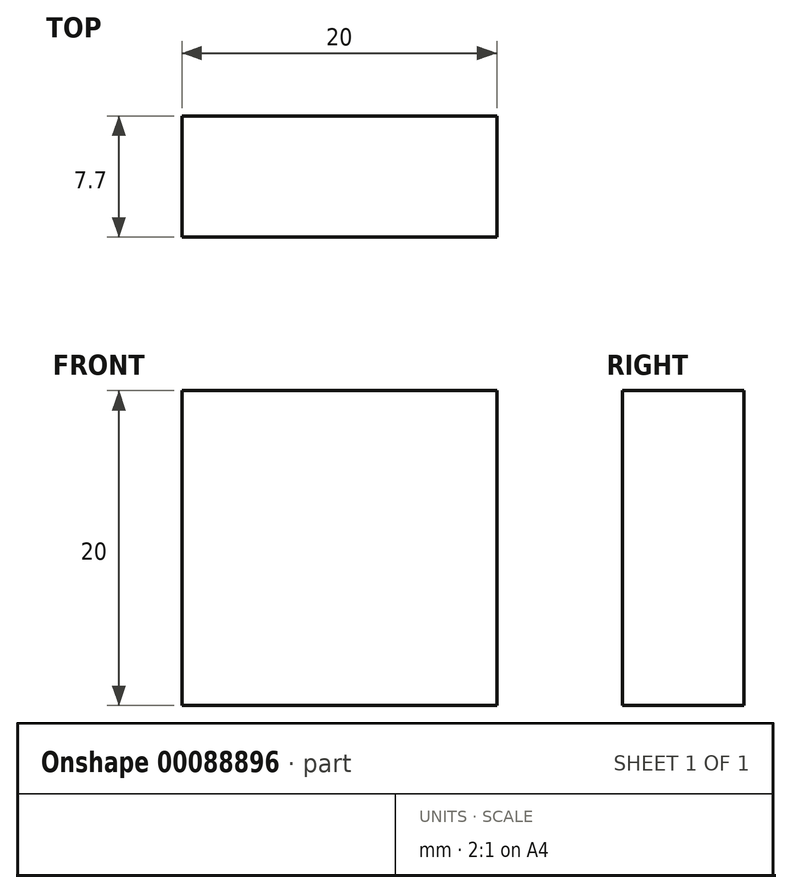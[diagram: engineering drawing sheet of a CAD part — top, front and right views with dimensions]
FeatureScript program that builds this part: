
annotation { "Feature Type Name" : "Feature", "Feature Type Description" : "" }
export const myFeature = defineFeature(function(context is Context, id is Id, definition is map)
    precondition{}
    {
        {
            var Q0;
            Q0=qCreatedBy(makeId("Front.planeOp"),FACE);
            var sketch = newSketch(context, id + "F0", { "sketchPlane" : qUnion([Q0])});
            skLineSegment(sketch, "E0.bottom", {"start": v(0, 0) * mm, "end": v(20, 0) * mm});
            skLineSegment(sketch, "E0.top", {"start": v(0, 20) * mm, "end": v(20, 20) * mm});
            skLineSegment(sketch, "E0.left", {"start": v(0, 0) * mm, "end": v(0, 20) * mm});
            skLineSegment(sketch, "E0.right", {"start": v(20, 0) * mm, "end": v(20, 20) * mm});
            skSolve(sketch);
        }
        {
            var Q0;
            Q0 = qSketchRegion(id + "F0", true);
            extrude(context, id + "F1", {"entities" : qUnion([Q0]), "depth" : 7.7 * mm});
        }
    });
